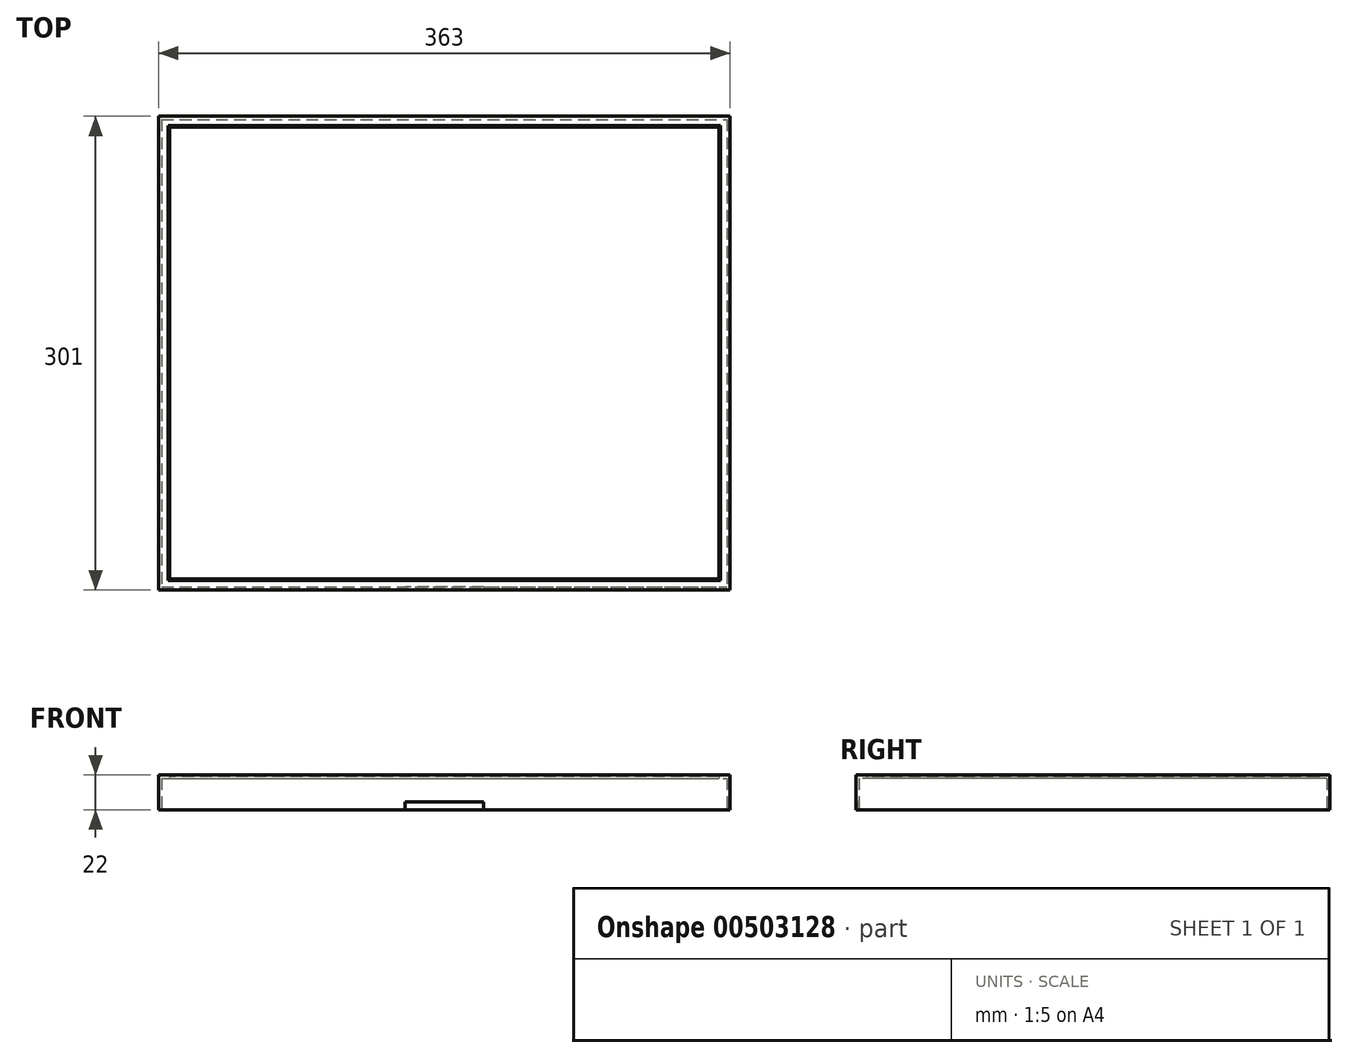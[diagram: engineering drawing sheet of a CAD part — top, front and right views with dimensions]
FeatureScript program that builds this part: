
annotation { "Feature Type Name" : "Feature", "Feature Type Description" : "" }
export const myFeature = defineFeature(function(context is Context, id is Id, definition is map)
    precondition{}
    {
        {
            var Q0;
            Q0=qCreatedBy(makeId("Top.planeOp"),FACE);
            var sketch = newSketch(context, id + "F0", { "sketchPlane" : qUnion([Q0])});
            skLineSegment(sketch, "E0.bottom", {"start": v(-179.5, 148.5) * mm, "end": v(179.5, 148.5) * mm});
            skLineSegment(sketch, "E0.top", {"start": v(-179.5, -148.5) * mm, "end": v(179.5, -148.5) * mm});
            skLineSegment(sketch, "E0.left", {"start": v(-179.5, 148.5) * mm, "end": v(-179.5, -148.5) * mm});
            skLineSegment(sketch, "E0.right", {"start": v(179.5, 148.5) * mm, "end": v(179.5, -148.5) * mm});
            skPoint(sketch, "E0.middle", {"position": v(0, 0) * mm});
            skLineSegment(sketch, "E1.bottom", {"start": v(-181.5, 150.5) * mm, "end": v(181.5, 150.5) * mm});
            skLineSegment(sketch, "E1.top", {"start": v(-181.5, -150.5) * mm, "end": v(181.5, -150.5) * mm});
            skLineSegment(sketch, "E1.left", {"start": v(-181.5, 150.5) * mm, "end": v(-181.5, -150.5) * mm});
            skLineSegment(sketch, "E1.right", {"start": v(181.5, 150.5) * mm, "end": v(181.5, -150.5) * mm});
            skLineSegment(sketch, "E2.bottom", {"start": v(-174.5, 143.5) * mm, "end": v(174.5, 143.5) * mm});
            skLineSegment(sketch, "E2.top", {"start": v(-174.5, -143.5) * mm, "end": v(174.5, -143.5) * mm});
            skLineSegment(sketch, "E2.left", {"start": v(-174.5, 143.5) * mm, "end": v(-174.5, -143.5) * mm});
            skLineSegment(sketch, "E2.right", {"start": v(174.5, 143.5) * mm, "end": v(174.5, -143.5) * mm});
            skSolve(sketch);
        }
        {
            var Q0;
            Q0=makeQuery(id+"F0.imprint","IMPRINT",FACE,{"disambiguationData":[TD([[makeQuery(id+"F0.imprint","IMPRINT",EDGE,{"derivedFrom":sQuery(id+"F0.wireOp",EDGE,"E0.bottom")}),1.0]])]});
            var Q1;
            Q1=makeQuery(id+"F0.imprint","IMPRINT",FACE,{"disambiguationData":[TD([[makeQuery(id+"F0.imprint","IMPRINT",EDGE,{"derivedFrom":sQuery(id+"F0.wireOp",EDGE,"E2.bottom")}),-1.0]])]});
            var Q2;
            Q2=makeQuery(id+"F0.imprint","IMPRINT",FACE,{"disambiguationData":[TD([[makeQuery(id+"F0.imprint","IMPRINT",EDGE,{"derivedFrom":sQuery(id+"F0.wireOp",EDGE,"E0.bottom")}),-1.0]])]});
            extrude(context, id + "F1", {"entities" : qUnion([Q0, Q1, Q2]), "depth" : 22 * mm});
        }
        {
            var Q0;
            Q0=makeQuery(id+"F0.imprint","IMPRINT",FACE,{"disambiguationData":[TD([[makeQuery(id+"F0.imprint","IMPRINT",EDGE,{"derivedFrom":sQuery(id+"F0.wireOp",EDGE,"E2.bottom")}),-1.0]])]});
            extrude(context, id + "F2", {"entities" : qUnion([Q0]), "operationType" : NewBodyOperationType.REMOVE, "depth" : 25 * mm});
        }
        {
            var Q0;
            Q0=makeQuery(id+"F0.imprint","IMPRINT",FACE,{"disambiguationData":[TD([[makeQuery(id+"F0.imprint","IMPRINT",EDGE,{"derivedFrom":sQuery(id+"F0.wireOp",EDGE,"E0.bottom")}),-1.0]])]});
            extrude(context, id + "F3", {"entities" : qUnion([Q0]), "operationType" : NewBodyOperationType.REMOVE, "depth" : 20 * mm});
        }
        {
            var Q0;
            Q0=makeQuery(id+"F2.boolean.opBoolean","INTERSECT",EDGE,{"derivedFrom":[makeQuery(id+"F1.opExtrude","CAP_FACE",FACE,{"disambiguationData":[OSD([sQuery(id+"F0.wireOp",EDGE,"E1.bottom"),sQuery(id+"F0.wireOp",EDGE,"E1.top"),sQuery(id+"F0.wireOp",EDGE,"E1.left"),sQuery(id+"F0.wireOp",EDGE,"E1.right")])],"isStart":false}),makeQuery(id+"F2.opExtrude","SWEPT_FACE",FACE,{"disambiguationData":[OSD([sQuery(id+"F0.wireOp",EDGE,"E2.top")])]})]});
            var Q1;
            Q1=makeQuery(id+"F2.boolean.opBoolean","INTERSECT",EDGE,{"derivedFrom":[makeQuery(id+"F1.opExtrude","CAP_FACE",FACE,{"disambiguationData":[OSD([sQuery(id+"F0.wireOp",EDGE,"E1.bottom"),sQuery(id+"F0.wireOp",EDGE,"E1.top"),sQuery(id+"F0.wireOp",EDGE,"E1.left"),sQuery(id+"F0.wireOp",EDGE,"E1.right")])],"isStart":false}),makeQuery(id+"F2.opExtrude","SWEPT_FACE",FACE,{"disambiguationData":[OSD([sQuery(id+"F0.wireOp",EDGE,"E2.left")])]})]});
            var Q2;
            Q2=makeQuery(id+"F2.boolean.opBoolean","INTERSECT",EDGE,{"derivedFrom":[makeQuery(id+"F1.opExtrude","CAP_FACE",FACE,{"disambiguationData":[OSD([sQuery(id+"F0.wireOp",EDGE,"E1.bottom"),sQuery(id+"F0.wireOp",EDGE,"E1.top"),sQuery(id+"F0.wireOp",EDGE,"E1.left"),sQuery(id+"F0.wireOp",EDGE,"E1.right")])],"isStart":false}),makeQuery(id+"F2.opExtrude","SWEPT_FACE",FACE,{"disambiguationData":[OSD([sQuery(id+"F0.wireOp",EDGE,"E2.bottom")])]})]});
            var Q3;
            Q3=makeQuery(id+"F2.boolean.opBoolean","INTERSECT",EDGE,{"derivedFrom":[makeQuery(id+"F1.opExtrude","CAP_FACE",FACE,{"disambiguationData":[OSD([sQuery(id+"F0.wireOp",EDGE,"E1.bottom"),sQuery(id+"F0.wireOp",EDGE,"E1.top"),sQuery(id+"F0.wireOp",EDGE,"E1.left"),sQuery(id+"F0.wireOp",EDGE,"E1.right")])],"isStart":false}),makeQuery(id+"F2.opExtrude","SWEPT_FACE",FACE,{"disambiguationData":[OSD([sQuery(id+"F0.wireOp",EDGE,"E2.right")])]})]});
            chamfer(context, id + "F4", {"entities" : qUnion([Q0, Q1, Q2, Q3]), "width" : 1 * mm, "tangentPropagation" : true});
        }
        {
            var Q0;
            Q0=makeQuery(id+"F1.opExtrude","SWEPT_FACE",FACE,{"disambiguationData":[OSD([sQuery(id+"F0.wireOp",EDGE,"E1.top")])]});
            var sketch = newSketch(context, id + "F5", { "sketchPlane" : qUnion([Q0])});
            skLineSegment(sketch, "E3.bottom", {"start": v(-25, 5) * mm, "end": v(25, 5) * mm});
            skLineSegment(sketch, "E3.top", {"start": v(-25, -5) * mm, "end": v(25, -5) * mm});
            skLineSegment(sketch, "E3.left", {"start": v(-25, 5) * mm, "end": v(-25, -5) * mm});
            skLineSegment(sketch, "E3.right", {"start": v(25, 5) * mm, "end": v(25, -5) * mm});
            skPoint(sketch, "E3.middle", {"position": v(0, 0) * mm});
            skSolve(sketch);
        }
        {
            var Q0;
            {var subQ0=sQuery(id+"F5.wireOp",EDGE,"E3.bottom");Q0=makeQuery(id+"F5.imprint","IMPRINT",FACE,{"disambiguationData":[TD([[makeQuery(id+"F5.imprint","IMPRINT",EDGE,{"derivedFrom":subQ0}),-1.0]])]});}
            extrude(context, id + "F6", {"entities" : qUnion([Q0]), "operationType" : NewBodyOperationType.REMOVE, "oppositeDirection" : true, "depth" : 25 * mm});
        }
    });
